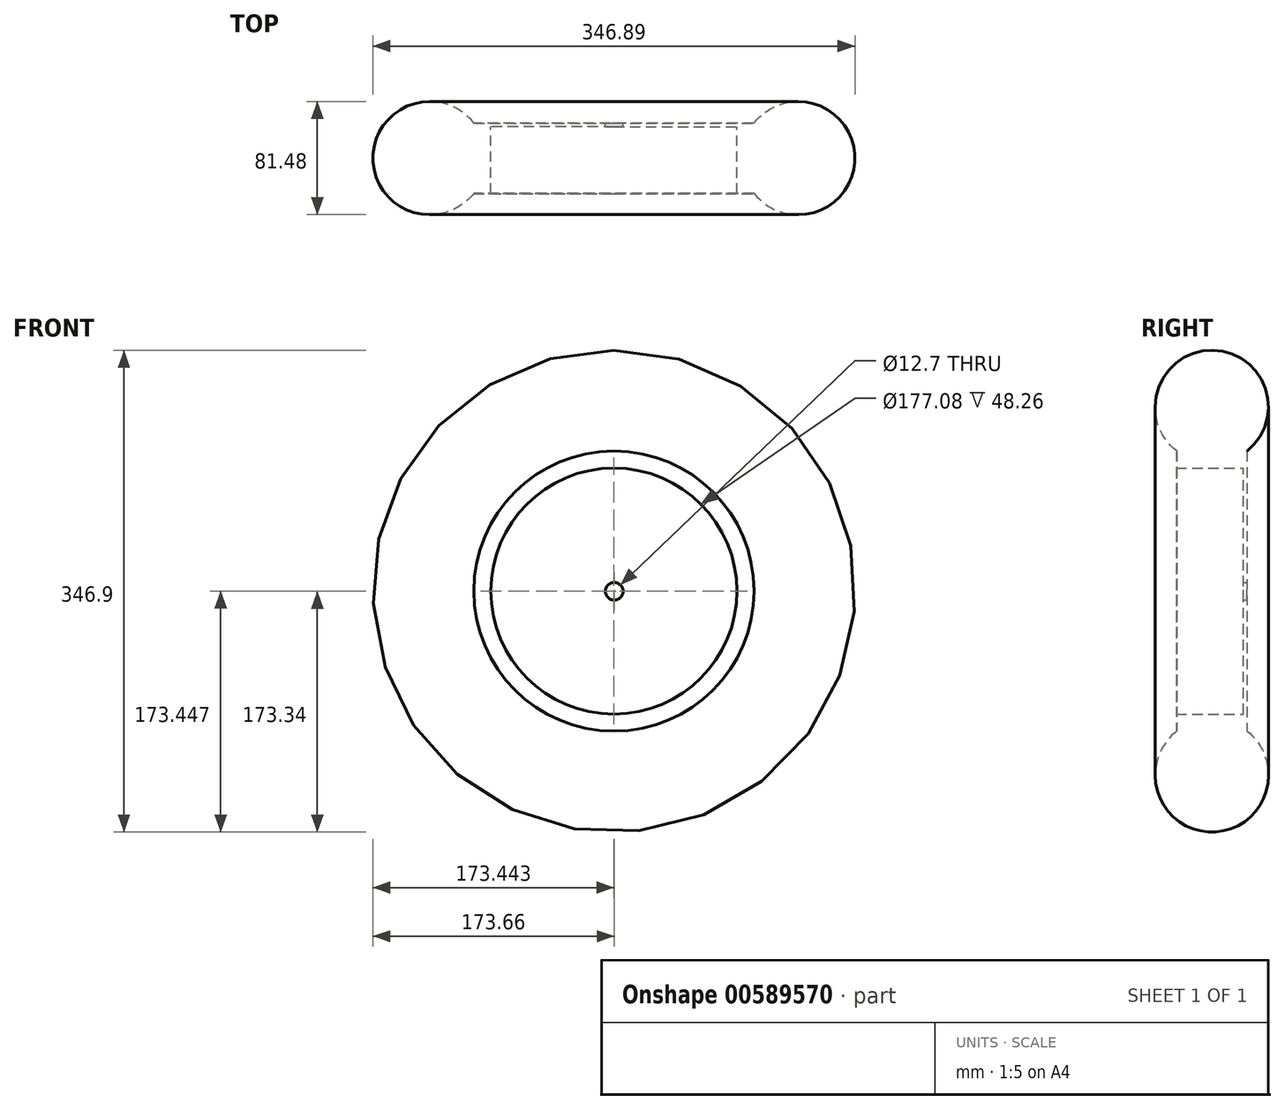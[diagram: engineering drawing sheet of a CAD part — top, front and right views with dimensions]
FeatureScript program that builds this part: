
annotation { "Feature Type Name" : "Feature", "Feature Type Description" : "" }
export const myFeature = defineFeature(function(context is Context, id is Id, definition is map)
    precondition{}
    {
        {
            var Q0;
            Q0=qCreatedBy(makeId("Front.planeOp"),FACE);
            var sketch = newSketch(context, id + "F0", { "sketchPlane" : qUnion([Q0])});
            skCircle(sketch, "E0", {"center": v(-0.22, 0.1) * mm, "radius": 88.9 * mm});
            skCircle(sketch, "E1", {"center": v(0, 0) * mm, "radius": 6.35 * mm});
            skSolve(sketch);
        }
        {
            var Q0;
            Q0=makeQuery(id+"F0.imprint","IMPRINT",FACE,{"disambiguationData":[TD([[makeQuery(id+"F0.imprint","IMPRINT",EDGE,{"derivedFrom":sQuery(id+"F0.wireOp",EDGE,"E0")}),1.0]])]});
            extrude(context, id + "F1", {"entities" : qUnion([Q0]), "depth" : 2.54 * mm, "offsetDistance" : 25.4 * mm});
        }
        {
            var Q0;
            Q0=qCreatedBy(makeId("Right.planeOp"),FACE);
            var sketch = newSketch(context, id + "F2", { "sketchPlane" : qUnion([Q0])});
            skLineSegment(sketch, "E2.bottom", {"start": v(-50.8, 100.94) * mm, "end": v(0, 100.94) * mm});
            skLineSegment(sketch, "E2.top", {"start": v(-50.8, 88.65) * mm, "end": v(0, 88.65) * mm});
            skLineSegment(sketch, "E2.left", {"start": v(-50.8, 100.94) * mm, "end": v(-50.8, 88.65) * mm});
            skLineSegment(sketch, "E2.right", {"start": v(0, 100.94) * mm, "end": v(0, 88.65) * mm});
            skCircle(sketch, "E3", {"center": v(-25.18, 132.81) * mm, "radius": 40.74 * mm});
            skSolve(sketch);
        }
        {
            var Q0;
            Q0 = qSketchRegion(id + "F2", true);
            var Q1;
            Q1=makeQuery(id+"F1.opExtrude","CAP_EDGE",EDGE,{"disambiguationData":[OSD([sQuery(id+"F0.wireOp",EDGE,"E0")])],"isStart":false});
            revolve(context, id + "F3", {"operationType" : NewBodyOperationType.ADD, "entities" : qUnion([Q0]), "axis" : qUnion([Q1]), "revolveType" : RevolveType.FULL});
        }
    });
